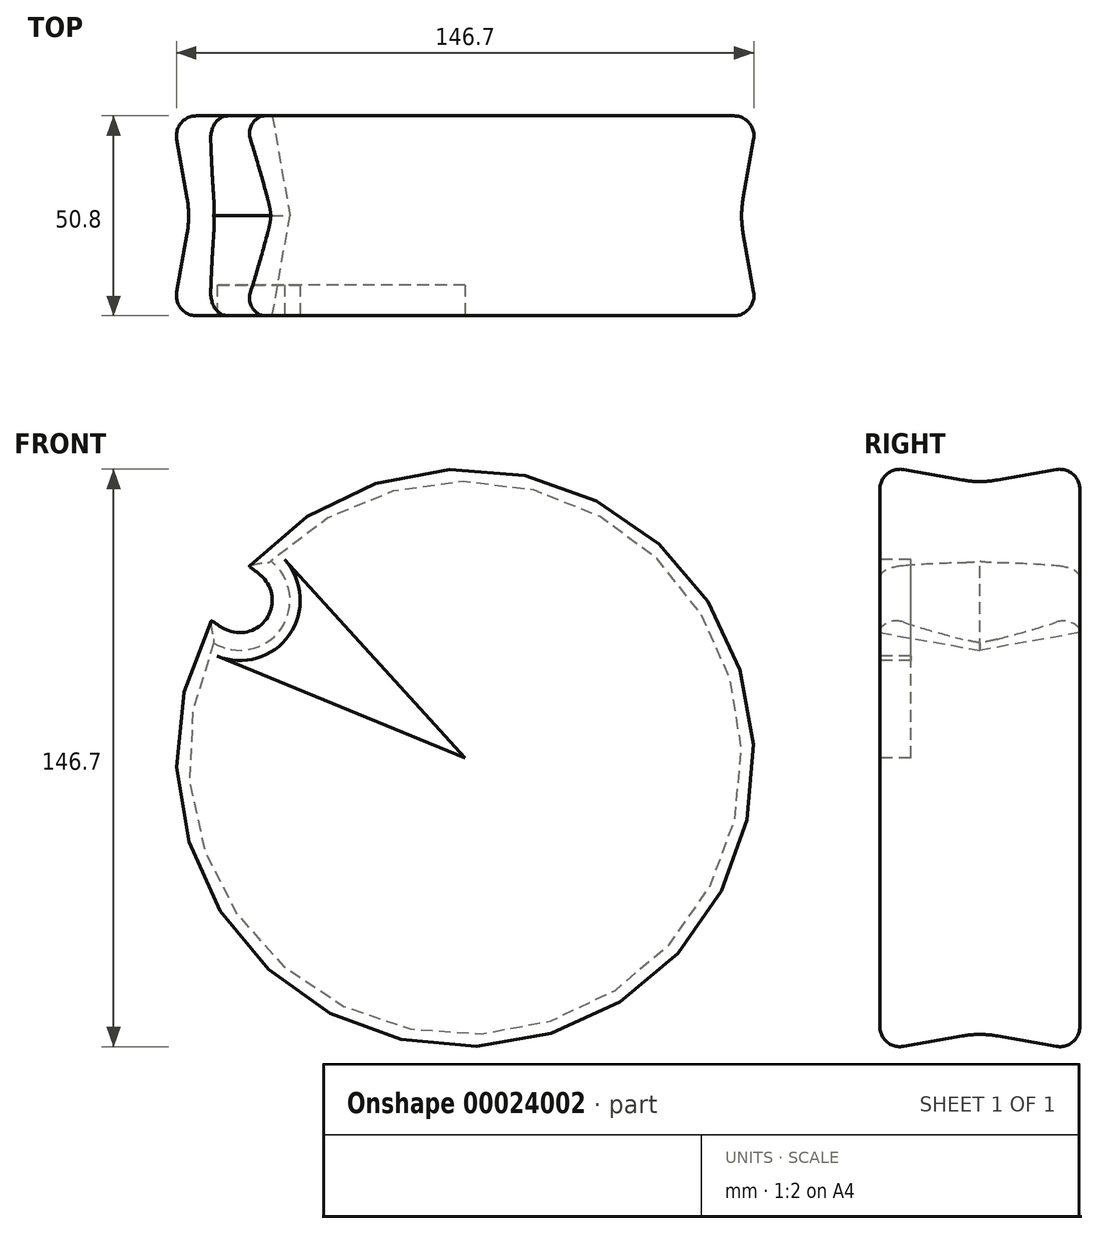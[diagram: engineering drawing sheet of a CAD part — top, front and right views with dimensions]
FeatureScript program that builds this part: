
annotation { "Feature Type Name" : "Feature", "Feature Type Description" : "" }
export const myFeature = defineFeature(function(context is Context, id is Id, definition is map)
    precondition{}
    {
        {
            var Q0;
            Q0=qCreatedBy(makeId("Front.planeOp"),FACE);
            var sketch = newSketch(context, id + "F0", { "sketchPlane" : qUnion([Q0])});
            skArc(sketch, "E0", {"start": v(-63.53, 29.04) * mm, "mid": v(57.22, -40.06) * mm, "end": v(-49.02, 49.76) * mm});
            skLineSegment(sketch, "E1", {"start": v(0, 0) * mm, "end": v(-57.22, 40.06) * mm, "construction": true});
            skArc(sketch, "E2", {"start": v(-63.53, 29.04) * mm, "mid": v(-46.81, 32.78) * mm, "end": v(-49.02, 49.76) * mm});
            skSolve(sketch);
        }
        {
            var Q0;
            Q0=makeQuery(id+"F0.imprint","IMPRINT",FACE,{"disambiguationData":[TD([[makeQuery(id+"F0.imprint","IMPRINT",EDGE,{"derivedFrom":sQuery(id+"F0.wireOp",EDGE,"E0")}),1.0]])]});
            extrude(context, id + "F1", {"entities" : qUnion([Q0]), "endBound" : BoundingType.SYMMETRIC, "depth" : 50.8 * mm, "hasDraft" : true, "draftAngle" : 10 * degree});
        }
        {
            var Q0;
            Q0=makeQuery(id+"F1.opExtrude","CAP_EDGE",EDGE,{"disambiguationData":[OSD([sQuery(id+"F0.wireOp",EDGE,"E0")])],"isStart":true});
            fillet(context, id + "F2", {"entities" : qUnion([Q0]), "radius" : 5.08 * mm, "tangentPropagation" : true, "allowEdgeOverflow" : false});
        }
        {
            var Q0;
            Q0=makeQuery(id+"F1.opExtrude","CAP_EDGE",EDGE,{"disambiguationData":[OSD([sQuery(id+"F0.wireOp",EDGE,"E0")])],"isStart":false});
            fillet(context, id + "F3", {"entities" : qUnion([Q0]), "radius" : 5.08 * mm, "tangentPropagation" : true, "allowEdgeOverflow" : false});
        }
        {
            var Q0;
            {var subQ0=makeQuery(id+"F1.opExtrude","SWEPT_FACE",FACE,{"disambiguationData":[OSD([sQuery(id+"F0.wireOp",EDGE,"E0")])]});Q0=makeQuery(id+"F1.*.booleanUnion.opBoolean","MERGE",EDGE,{"derivedFrom":[makeQuery(id+"F1.*.split.splitOp","SPLIT_SURFACE_INTERSECT",EDGE,{"derivedFrom":[subQ0]}),makeQuery(id+"F1.*.split.splitOp","SPLIT_SURFACE_INTERSECT",EDGE,{"derivedFrom":[subQ0],"isFromBackBody":true})]});}
            fillet(context, id + "F4", {"entities" : qUnion([Q0]), "radius" : 25.4 * mm, "tangentPropagation" : true, "allowEdgeOverflow" : false});
        }
        {
            var Q0;
            Q0=makeQuery(id+"F1.opExtrude","CAP_FACE",FACE,{"disambiguationData":[OSD([sQuery(id+"F0.wireOp",EDGE,"E0"),sQuery(id+"F0.wireOp",EDGE,"E2")])],"isStart":false});
            var sketch = newSketch(context, id + "F5", { "sketchPlane" : qUnion([Q0])});
            skArc(sketch, "E3", {"start": v(-63.04, 25.9) * mm, "mid": v(-44.67, 31.28) * mm, "end": v(-45.9, 50.38) * mm});
            skLineSegment(sketch, "E4", {"start": v(0, 0) * mm, "end": v(-45.9, 50.38) * mm});
            skLineSegment(sketch, "E5", {"start": v(0, 0) * mm, "end": v(-63.04, 25.9) * mm});
            skSolve(sketch);
        }
        {
            var Q0;
            Q0=makeQuery(id+"F5.imprint","IMPRINT",FACE,{"disambiguationData":[TD([[makeQuery(id+"F5.imprint","IMPRINT",EDGE,{"derivedFrom":sQuery(id+"F5.wireOp",EDGE,"E3")}),-1.0]])]});
            extrude(context, id + "F6", {"entities" : qUnion([Q0]), "operationType" : NewBodyOperationType.REMOVE, "oppositeDirection" : true, "depth" : 7.84 * mm});
        }
    });
